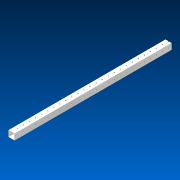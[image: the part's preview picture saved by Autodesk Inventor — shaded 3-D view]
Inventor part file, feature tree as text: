
AUTODESK INVENTOR PART (.ipt)
format: ipt  version: 2022.2 (Build 262287000, 287)  size: 862,208 bytes
history: native  units: in
note: dims shown in document units (in); Inventor stores cm internally (conversion verified against a paired STEP export)
features: other x52, pattern_linear x2, extrude x1, sketch x1
ambient origin geometry x8: Origin, YZ Plane, XZ Plane, XY Plane, X Axis, Y Axis, Z Axis, Center Point
bodies: Solid1 (feature_tree)
feature tree (56):
  extrude  "Extrusion1"  TaperAngle=0.0deg  [1 undecoded]
  other  "Work Axis1"
  other  "Work Axis2"
  pattern_linear  "Rectangular Pattern1"  Count1=26  [1 undecoded]
  pattern_linear  "Rectangular Pattern2"  Spacing1=1.0in  [1 undecoded]
  sketch  "Sketch1"  dims[d0=33.0in d1=0.0in d2=10.2362in d4=1.0in d5=9.8425in d7=1.0in]
  other  "Work Axis3"
  other  "Work Axis4"
  other  "Work Axis5"
  other  "Work Axis6"
  other  "Work Axis7"
  other  "Work Axis8"
  other  "Work Axis9"
  other  "Work Axis10"
  other  "Work Axis11"
  other  "Work Axis12"
  other  "Work Axis13"
  other  "Work Axis14"
  other  "Work Axis15"
  other  "Work Axis16"
  other  "Work Axis17"
  other  "Work Axis18"
  other  "Work Axis19"
  other  "Work Axis20"
  other  "Work Axis21"
  other  "Work Axis22"
  other  "Work Axis23"
  other  "Work Axis24"
  other  "Work Axis25"
  other  "Work Axis26"
  other  "Work Axis27"
  other  "Work Axis28"
  other  "Work Axis29"
  other  "Work Axis63"
  other  "Work Axis64"
  other  "Work Axis65"
  other  "Work Axis66"
  other  "Work Axis67"
  other  "Work Axis68"
  other  "Work Axis69"
  other  "Work Axis70"
  other  "Work Axis71"
  other  "Work Axis72"
  other  "Work Axis73"
  other  "Work Axis74"
  other  "Work Axis75"
  other  "Work Axis76"
  other  "Work Axis77"
  other  "Work Axis78"
  other  "Work Axis79"
  other  "Work Axis80"
  other  "Work Axis81"
  other  "Work Axis82"
  other  "Work Axis83"
  other  "Work Axis84"
  other  "LPattern2"
note: 3 required parameter values undecoded (feature->parameter linkage not recoverable at this tier; creation-order binding heuristic only, values carry confidence <= 0.55)
